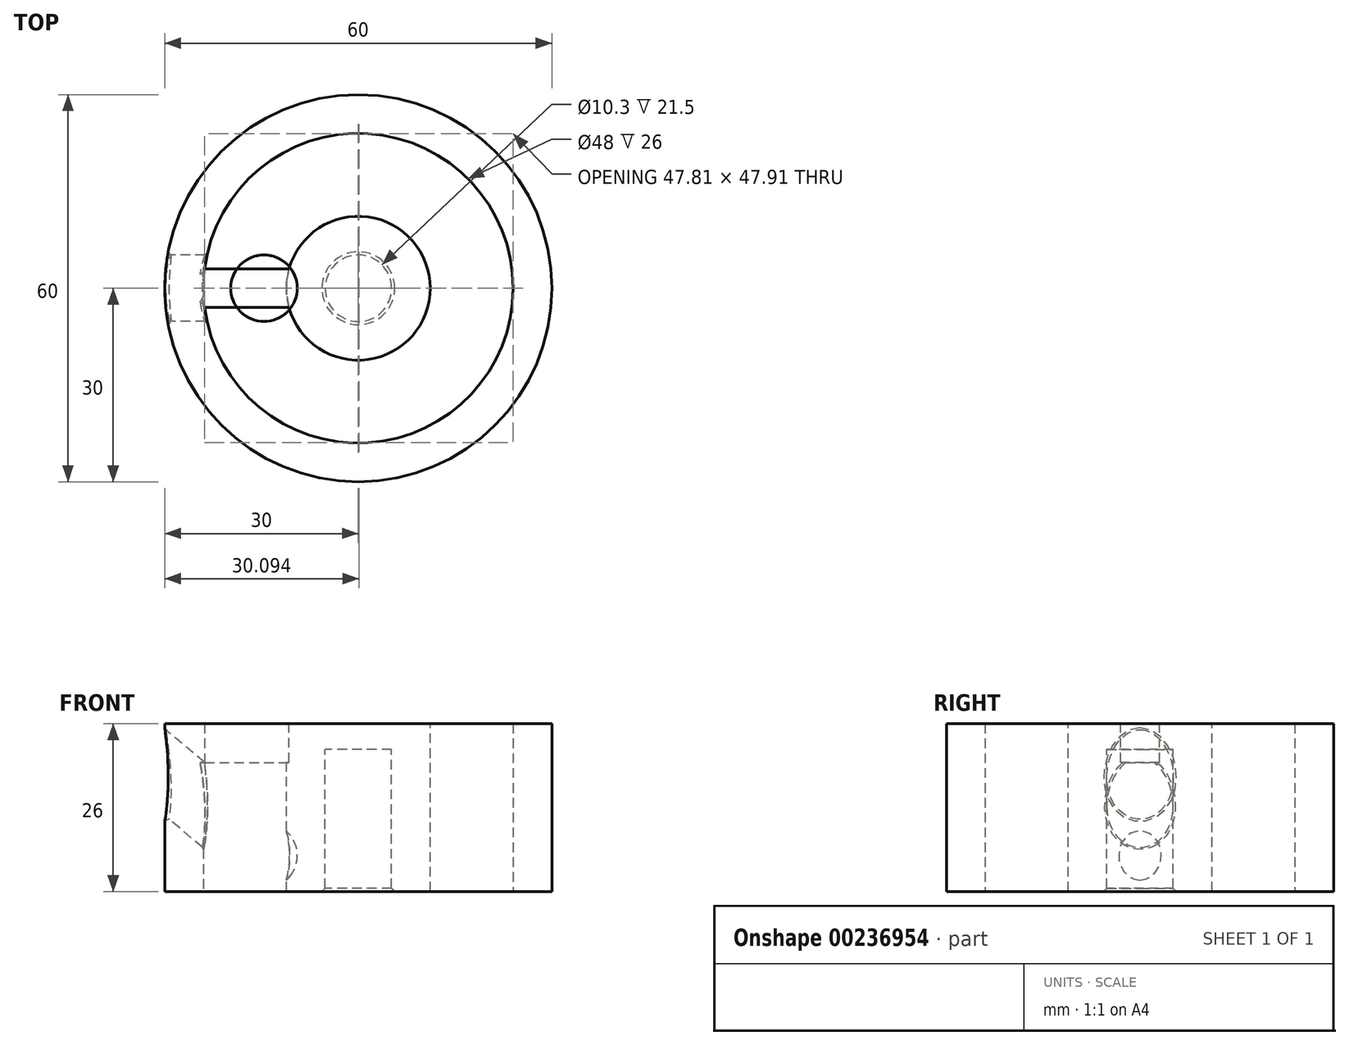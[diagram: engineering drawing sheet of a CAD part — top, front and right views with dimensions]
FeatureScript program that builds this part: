
annotation { "Feature Type Name" : "Feature", "Feature Type Description" : "" }
export const myFeature = defineFeature(function(context is Context, id is Id, definition is map)
    precondition{}
    {
        {
            var Q0;
            Q0=qCreatedBy(makeId("Top.planeOp"),FACE);
            var sketch = newSketch(context, id + "F0", { "sketchPlane" : qUnion([Q0])});
            skCircle(sketch, "E0", {"center": v(0, 0) * mm, "radius": 30 * mm});
            skCircle(sketch, "E1", {"center": v(0, 0) * mm, "radius": 24 * mm});
            skSolve(sketch);
        }
        {
            var Q0;
            Q0 = qSketchRegion(id + "F0", true);
            extrude(context, id + "F1", {"entities" : qUnion([Q0]), "depth" : 26 * mm});
        }
        {
            var Q0;
            Q0=makeQuery(id+"F1.opExtrude","CAP_FACE",FACE,{"disambiguationData":[OSD([sQuery(id+"F0.wireOp",EDGE,"E0"),sQuery(id+"F0.wireOp",EDGE,"E1")])],"isStart":false});
            var sketch = newSketch(context, id + "F2", { "sketchPlane" : qUnion([Q0])});
            skCircle(sketch, "E2", {"center": v(0, 0) * mm, "radius": 5.15 * mm});
            skCircle(sketch, "E3", {"center": v(0, 0) * mm, "radius": 11.15 * mm});
            skSolve(sketch);
        }
        {
            var Q0;
            Q0 = qSketchRegion(id + "F2", true);
            extrude(context, id + "F3", {"entities" : qUnion([Q0]), "oppositeDirection" : true, "depth" : 26 * mm});
        }
        {
            var Q0;
            Q0=makeQuery(id+"F3.opExtrude","CAP_FACE",FACE,{"disambiguationData":[OSD([sQuery(id+"F2.wireOp",EDGE,"E2"),sQuery(id+"F2.wireOp",EDGE,"E3")])],"isStart":true});
            var sketch = newSketch(context, id + "F4", { "sketchPlane" : qUnion([Q0])});
            skLineSegment(sketch, "E4.bottom", {"start": v(-25.8, 3) * mm, "end": v(3.5, 3) * mm});
            skLineSegment(sketch, "E4.top", {"start": v(-25.8, -3) * mm, "end": v(3.5, -3) * mm});
            skLineSegment(sketch, "E4.left", {"start": v(-25.8, 3) * mm, "end": v(-25.8, -3) * mm});
            skLineSegment(sketch, "E4.right", {"start": v(3.5, 3) * mm, "end": v(3.5, -3) * mm});
            skPoint(sketch, "E4.middle", {"position": v(-11.15, 0) * mm});
            skSolve(sketch);
        }
        {
            var Q0;
            {var subQ0=sQuery(id+"F4.wireOp",EDGE,"E4.left");Q0=makeQuery(id+"F4.imprint","IMPRINT",FACE,{"disambiguationData":[TD([[makeQuery(id+"F4.imprint","IMPRINT",EDGE,{"derivedFrom":subQ0}),1.0]])]});}
            extrude(context, id + "F5", {"entities" : qUnion([Q0]), "operationType" : NewBodyOperationType.ADD, "oppositeDirection" : true, "depth" : 6 * mm});
        }
        {
            var Q0;
            Q0=qCreatedBy(makeId("Front.planeOp"),FACE);
            var sketch = newSketch(context, id + "F6", { "sketchPlane" : qUnion([Q0])});
            skLineSegment(sketch, "E5.0", {"start": v(-30, 26) * mm, "end": v(30, 26) * mm});
            skLineSegment(sketch, "E6", {"start": v(-30, 0) * mm, "end": v(-30, 26) * mm});
            skLineSegment(sketch, "E7", {"start": v(30, 26) * mm, "end": v(30, 0) * mm});
            skLineSegment(sketch, "E8.0", {"start": v(-30, 0) * mm, "end": v(30, 0) * mm});
            skLineSegment(sketch, "E9", {"start": v(-30, 25.2) * mm, "end": v(-11.3, 9.52) * mm});
            skLineSegment(sketch, "E10", {"start": v(-10.67, 2.26) * mm, "end": v(-10.67, 2.26) * mm});
            skLineSegment(sketch, "E11", {"start": v(-17.93, 1.63) * mm, "end": v(-36.62, 17.3) * mm});
            skLineSegment(sketch, "E12", {"start": v(-36.62, 17.3) * mm, "end": v(-30, 25.2) * mm});
            skPoint(sketch, "E13.visualSharp", {"position": v(-7.36, 6.2) * mm});
            skArc(sketch, "E13.filletArc", {"start": v(-10.67, 2.26) * mm, "mid": v(-9.49, 6.02) * mm, "end": v(-11.3, 9.52) * mm});
            skPoint(sketch, "E14.visualSharp", {"position": v(-13.98, -1.68) * mm});
            skArc(sketch, "E14.filletArc", {"start": v(-17.93, 1.63) * mm, "mid": v(-14.17, 0.44) * mm, "end": v(-10.67, 2.26) * mm});
            skLineSegment(sketch, "E15", {"start": v(-10.67, 2.26) * mm, "end": v(-33.31, 21.25) * mm});
            skSolve(sketch);
        }
        {
            var Q0;
            {var subQ0=sQuery(id+"F6.wireOp",EDGE,"E9");Q0=makeQuery(id+"F6.imprint","IMPRINT",FACE,{"disambiguationData":[TD([[makeQuery(id+"F6.imprint","IMPRINT",EDGE,{"derivedFrom":subQ0}),-1.0]])]});}
            var Q1;
            {var subQ0=sQuery(id+"F6.wireOp",EDGE,"E12");var subQ3=sQuery(id+"F6.wireOp",EDGE,"E15");var subQ5=makeQuery(id+"F6.imprint","INTERSECT",VERTEX,{"derivedFrom":[subQ0,subQ3]});Q1=makeQuery(id+"F6.imprint","IMPRINT",FACE,{"disambiguationData":[TD([[makeQuery(id+"F6.imprint","IMPRINT",EDGE,{"disambiguationData":[TD([[subQ5,1.0]])],"derivedFrom":subQ3}),-1.0]])]});}
            var Q2;
            Q2=sQuery(id+"F6.wireOp",EDGE,"E15");
            revolve(context, id + "F7", {"operationType" : NewBodyOperationType.REMOVE, "entities" : qUnion([Q0, Q1]), "axis" : qUnion([Q2]), "revolveType" : RevolveType.FULL, "oppositeDirection" : true});
        }
        {
            var Q0;
            {var subQ0=sQuery(id+"F4.wireOp",EDGE,"E4.left");var subQ1=sQuery(id+"F4.wireOp",EDGE,"E4.top");var subQ2=sQuery(id+"F4.wireOp",EDGE,"E4.bottom");var subQ3=sQuery(id+"F2.wireOp",EDGE,"E3");Q0=makeQuery(id+"Fs8iNR6dOOuEdMG_1.2.F5.boolean.opBoolean","MERGE",FACE,{"derivedFrom":[makeQuery(id+"Fs8iNR6dOOuEdMG_1.1.F5.boolean.opBoolean","MERGE",FACE,{"derivedFrom":[makeQuery(id+"F5.boolean.opBoolean","MERGE",FACE,{"derivedFrom":[makeQuery(id+"F1.opExtrude","CAP_FACE",FACE,{"disambiguationData":[OSD([sQuery(id+"F0.wireOp",EDGE,"E0"),sQuery(id+"F0.wireOp",EDGE,"E1")])],"isStart":false}),makeQuery(id+"F3.opExtrude","CAP_FACE",FACE,{"disambiguationData":[OSD([sQuery(id+"F2.wireOp",EDGE,"E2"),subQ3])],"isStart":true}),makeQuery(id+"F5.opExtrude","CAP_FACE",FACE,{"disambiguationData":[OSD([subQ3,subQ2,subQ1,subQ0])],"isStart":true})]}),makeQuery(id+"Fs8iNR6dOOuEdMG_1.1.F5.opExtrude","CAP_FACE",FACE,{"disambiguationData":[OSD([subQ3,subQ2,subQ1,subQ0])],"isStart":true})]}),makeQuery(id+"Fs8iNR6dOOuEdMG_1.2.F5.opExtrude","CAP_FACE",FACE,{"disambiguationData":[OSD([subQ3,subQ2,subQ1,subQ0])],"isStart":true})]});}
            var sketch = newSketch(context, id + "F8", { "sketchPlane" : qUnion([Q0])});
            skCircle(sketch, "E16", {"center": v(0, 0) * mm, "radius": 7.63 * mm});
            skSolve(sketch);
        }
        {
            var Q0;
            Q0 = qSketchRegion(id + "F8", true);
            extrude(context, id + "F9", {"entities" : qUnion([Q0]), "operationType" : NewBodyOperationType.ADD, "oppositeDirection" : true, "depth" : 4 * mm});
        }
        {
            var Q0;
            Q0=makeQuery(id+"Fc7FvZwjBquzWQh_1.1.F7.boolean.opBoolean","INTERSECT",EDGE,{"derivedFrom":[makeQuery(id+"F1.opExtrude","SWEPT_FACE",FACE,{"disambiguationData":[OSD([sQuery(id+"F0.wireOp",EDGE,"E0")])]}),makeQuery(id+"Fc7FvZwjBquzWQh_1.1.F7.opRevolve","SWEPT_FACE",FACE,{"disambiguationData":[OSD([sQuery(id+"F6.wireOp",EDGE,"E9")])]})]});
            var Q1;
            Q1=makeQuery(id+"Fc7FvZwjBquzWQh_1.1.F7.boolean.opBoolean","INTERSECT",EDGE,{"derivedFrom":[makeQuery(id+"F1.opExtrude","SWEPT_FACE",FACE,{"disambiguationData":[OSD([sQuery(id+"F0.wireOp",EDGE,"E1")])]}),makeQuery(id+"Fc7FvZwjBquzWQh_1.1.F7.opRevolve","SWEPT_FACE",FACE,{"disambiguationData":[OSD([sQuery(id+"F6.wireOp",EDGE,"E9")])]})]});
            var Q2;
            Q2=makeQuery(id+"F7.boolean.opBoolean","INTERSECT",EDGE,{"derivedFrom":[makeQuery(id+"F1.opExtrude","SWEPT_FACE",FACE,{"disambiguationData":[OSD([sQuery(id+"F0.wireOp",EDGE,"E0")])]}),makeQuery(id+"F7.opRevolve","SWEPT_FACE",FACE,{"disambiguationData":[OSD([sQuery(id+"F6.wireOp",EDGE,"E9")])]})]});
            var Q3;
            Q3=makeQuery(id+"F7.boolean.opBoolean","INTERSECT",EDGE,{"derivedFrom":[makeQuery(id+"F1.opExtrude","SWEPT_FACE",FACE,{"disambiguationData":[OSD([sQuery(id+"F0.wireOp",EDGE,"E1")])]}),makeQuery(id+"F7.opRevolve","SWEPT_FACE",FACE,{"disambiguationData":[OSD([sQuery(id+"F6.wireOp",EDGE,"E9")])]})]});
            var Q4;
            Q4=makeQuery(id+"Fc7FvZwjBquzWQh_1.2.F7.boolean.opBoolean","INTERSECT",EDGE,{"derivedFrom":[makeQuery(id+"F1.opExtrude","SWEPT_FACE",FACE,{"disambiguationData":[OSD([sQuery(id+"F0.wireOp",EDGE,"E1")])]}),makeQuery(id+"Fc7FvZwjBquzWQh_1.2.F7.opRevolve","SWEPT_FACE",FACE,{"disambiguationData":[OSD([sQuery(id+"F6.wireOp",EDGE,"E9")])]})]});
            var Q5;
            Q5=makeQuery(id+"Fc7FvZwjBquzWQh_1.2.F7.boolean.opBoolean","INTERSECT",EDGE,{"derivedFrom":[makeQuery(id+"F1.opExtrude","SWEPT_FACE",FACE,{"disambiguationData":[OSD([sQuery(id+"F0.wireOp",EDGE,"E0")])]}),makeQuery(id+"Fc7FvZwjBquzWQh_1.2.F7.opRevolve","SWEPT_FACE",FACE,{"disambiguationData":[OSD([sQuery(id+"F6.wireOp",EDGE,"E9")])]})]});
            chamfer(context, id + "F10", {"entities" : qUnion([Q0, Q1, Q2, Q3, Q4, Q5]), "width" : 0.4 * mm, "tangentPropagation" : true});
        }
        {
            var Q0;
            Q0=makeQuery(id+"F3.opExtrude","CAP_EDGE",EDGE,{"disambiguationData":[OSD([sQuery(id+"F2.wireOp",EDGE,"E2")])],"isStart":false});
            chamfer(context, id + "F11", {"entities" : qUnion([Q0]), "width" : 0.5 * mm, "tangentPropagation" : true});
        }
    });
